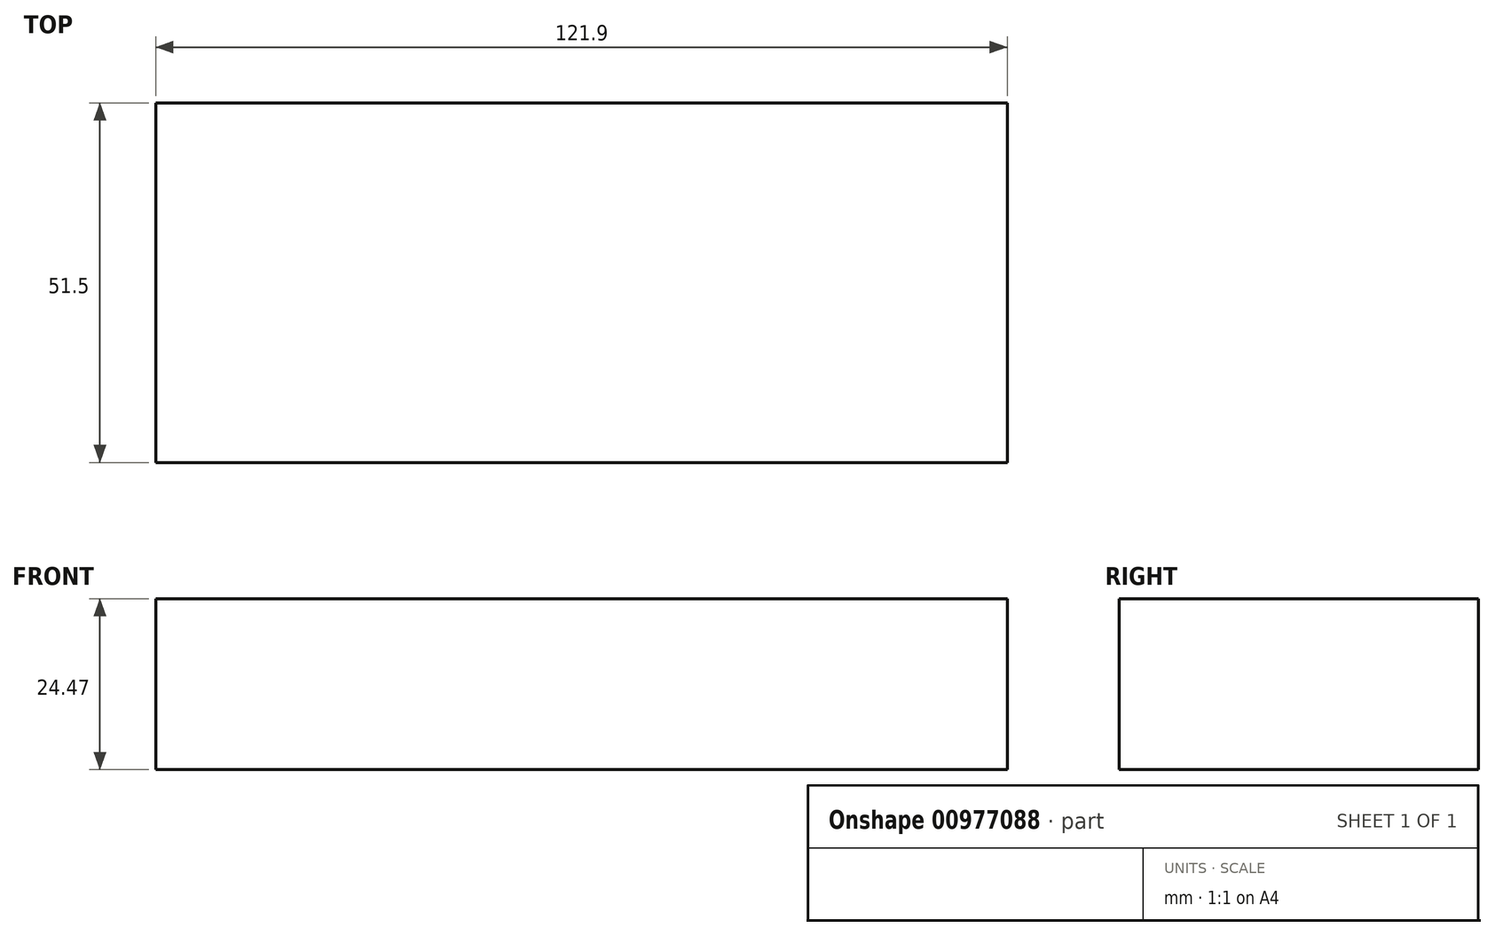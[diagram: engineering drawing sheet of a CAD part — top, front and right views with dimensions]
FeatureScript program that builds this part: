
annotation { "Feature Type Name" : "Feature", "Feature Type Description" : "" }
export const myFeature = defineFeature(function(context is Context, id is Id, definition is map)
    precondition{}
    {
        {
            var Q0;
            Q0=qCreatedBy(makeId("Top.planeOp"),FACE);
            var sketch = newSketch(context, id + "F0", { "sketchPlane" : qUnion([Q0])});
            skLineSegment(sketch, "E0.bottom", {"start": v(-60.95, 25.75) * mm, "end": v(60.95, 25.75) * mm});
            skLineSegment(sketch, "E0.top", {"start": v(-60.95, -25.75) * mm, "end": v(60.95, -25.75) * mm});
            skLineSegment(sketch, "E0.left", {"start": v(-60.95, 25.75) * mm, "end": v(-60.95, -25.75) * mm});
            skLineSegment(sketch, "E0.right", {"start": v(60.95, 25.75) * mm, "end": v(60.95, -25.75) * mm});
            skPoint(sketch, "E0.middle", {"position": v(0, 0) * mm});
            skSolve(sketch);
        }
        {
            var Q0;
            Q0=makeQuery(id+"F0.imprint","IMPRINT",FACE,{"disambiguationData":[TD([[makeQuery(id+"F0.imprint","IMPRINT",EDGE,{"derivedFrom":sQuery(id+"F0.wireOp",EDGE,"E0.bottom")}),-1.0]])]});
            extrude(context, id + "F1", {"entities" : qUnion([Q0]), "depth" : 24.47 * mm, "offsetDistance" : 25.4 * mm});
        }
    });
